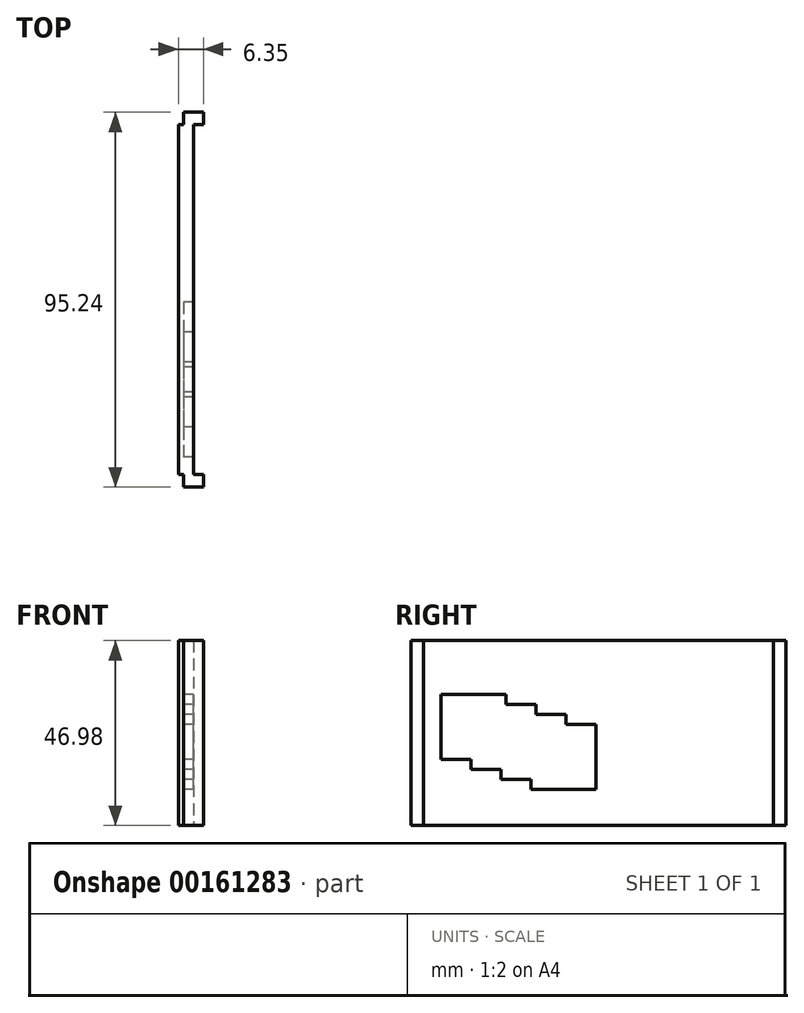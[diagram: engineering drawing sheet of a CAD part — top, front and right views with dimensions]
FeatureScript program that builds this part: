
annotation { "Feature Type Name" : "Feature", "Feature Type Description" : "" }
export const myFeature = defineFeature(function(context is Context, id is Id, definition is map)
    precondition{}
    {
        {
            var Q0;
            Q0=qCreatedBy(makeId("Right.planeOp"),FACE);
            var sketch = newSketch(context, id + "F0", { "sketchPlane" : qUnion([Q0])});
            skLineSegment(sketch, "E0.bottom", {"start": v(47.62, 23.5) * mm, "end": v(-47.63, 23.5) * mm});
            skLineSegment(sketch, "E0.top", {"start": v(47.63, -23.5) * mm, "end": v(-47.62, -23.5) * mm});
            skLineSegment(sketch, "E0.left", {"start": v(47.62, 23.5) * mm, "end": v(47.63, -23.5) * mm});
            skLineSegment(sketch, "E0.right", {"start": v(-47.63, 23.5) * mm, "end": v(-47.62, -23.5) * mm});
            skPoint(sketch, "E0.middle", {"position": v(0, 0) * mm});
            skLineSegment(sketch, "E1.bottom", {"start": v(-0.64, -14.35) * mm, "end": v(-17.14, -14.35) * mm});
            skLineSegment(sketch, "E1.top", {"start": v(-0.64, 2.16) * mm, "end": v(-17.15, 2.16) * mm});
            skLineSegment(sketch, "E1.left", {"start": v(-0.64, -14.35) * mm, "end": v(-0.64, 2.16) * mm});
            skLineSegment(sketch, "E1.right", {"start": v(-17.14, -14.35) * mm, "end": v(-17.15, 2.16) * mm});
            skPoint(sketch, "E1.middle", {"position": v(-8.9, -6.1) * mm});
            skLineSegment(sketch, "E2.bottom", {"start": v(-8.25, -11.81) * mm, "end": v(-24.77, -11.81) * mm});
            skLineSegment(sketch, "E2.top", {"start": v(-8.25, 4.7) * mm, "end": v(-24.77, 4.7) * mm});
            skLineSegment(sketch, "E2.left", {"start": v(-8.25, -11.81) * mm, "end": v(-8.25, 4.7) * mm});
            skLineSegment(sketch, "E2.right", {"start": v(-24.76, -11.81) * mm, "end": v(-24.77, 4.7) * mm});
            skLineSegment(sketch, "E3.bottom", {"start": v(-15.87, -9.27) * mm, "end": v(-32.38, -9.27) * mm});
            skLineSegment(sketch, "E3.top", {"start": v(-15.87, 7.24) * mm, "end": v(-32.38, 7.24) * mm});
            skLineSegment(sketch, "E3.left", {"start": v(-15.87, -9.27) * mm, "end": v(-15.87, 7.24) * mm});
            skLineSegment(sketch, "E3.right", {"start": v(-32.38, -9.27) * mm, "end": v(-32.38, 7.24) * mm});
            skLineSegment(sketch, "E4.bottom", {"start": v(-23.5, -6.73) * mm, "end": v(-40, -6.73) * mm});
            skLineSegment(sketch, "E4.top", {"start": v(-23.5, 9.78) * mm, "end": v(-40, 9.78) * mm});
            skLineSegment(sketch, "E4.left", {"start": v(-23.5, -6.73) * mm, "end": v(-23.5, 9.78) * mm});
            skLineSegment(sketch, "E4.right", {"start": v(-40, -6.73) * mm, "end": v(-40, 9.78) * mm});
            skSolve(sketch);
        }
        {
            var Q0;
            Q0=makeQuery(id+"F0.imprint","IMPRINT",FACE,{"disambiguationData":[TD([[makeQuery(id+"F0.imprint","IMPRINT",EDGE,{"derivedFrom":sQuery(id+"F0.wireOp",EDGE,"E0.bottom")}),1.0]])]});
            extrude(context, id + "F1", {"entities" : qUnion([Q0]), "depth" : 2.54 * mm});
        }
        {
            var Q0;
            Q0=makeQuery(id+"F1.opExtrude","CAP_FACE",FACE,{"disambiguationData":[OSD([sQuery(id+"F0.wireOp",EDGE,"E0.bottom"),sQuery(id+"F0.wireOp",EDGE,"E0.top"),sQuery(id+"F0.wireOp",EDGE,"E0.left"),sQuery(id+"F0.wireOp",EDGE,"E0.right"),sQuery(id+"F0.wireOp",EDGE,"E1.bottom"),sQuery(id+"F0.wireOp",EDGE,"E1.top"),sQuery(id+"F0.wireOp",EDGE,"E1.right"),sQuery(id+"F0.wireOp",EDGE,"db3a154d-421c-442b-b8d2-4df29128a182.bottom"),sQuery(id+"F0.wireOp",EDGE,"db3a154d-421c-442b-b8d2-4df29128a182.top"),sQuery(id+"F0.wireOp",EDGE,"db3a154d-421c-442b-b8d2-4df29128a182.left"),sQuery(id+"F0.wireOp",EDGE,"db3a154d-421c-442b-b8d2-4df29128a182.right"),sQuery(id+"F0.wireOp",EDGE,"fd7c79ed-5d07-4375-ac7c-8445cbfff98b.bottom"),sQuery(id+"F0.wireOp",EDGE,"fd7c79ed-5d07-4375-ac7c-8445cbfff98b.top"),sQuery(id+"F0.wireOp",EDGE,"fd7c79ed-5d07-4375-ac7c-8445cbfff98b.left"),sQuery(id+"F0.wireOp",EDGE,"fd7c79ed-5d07-4375-ac7c-8445cbfff98b.right"),sQuery(id+"F0.wireOp",EDGE,"f020ca0c-2cd2-49f9-a436-e8fc56810917.bottom"),sQuery(id+"F0.wireOp",EDGE,"f020ca0c-2cd2-49f9-a436-e8fc56810917.top"),sQuery(id+"F0.wireOp",EDGE,"f020ca0c-2cd2-49f9-a436-e8fc56810917.left"),sQuery(id+"F0.wireOp",EDGE,"f020ca0c-2cd2-49f9-a436-e8fc56810917.right")])],"isStart":true});
            var sketch = newSketch(context, id + "F2", { "sketchPlane" : qUnion([Q0])});
            skLineSegment(sketch, "E5.bottom", {"start": v(44.45, 23.5) * mm, "end": v(-44.45, 23.5) * mm});
            skLineSegment(sketch, "E5.top", {"start": v(44.45, -23.5) * mm, "end": v(-44.45, -23.5) * mm});
            skLineSegment(sketch, "E5.left", {"start": v(44.45, 23.5) * mm, "end": v(44.45, -23.5) * mm});
            skLineSegment(sketch, "E5.right", {"start": v(-44.45, 23.5) * mm, "end": v(-44.45, -23.5) * mm});
            skPoint(sketch, "E5.middle", {"position": v(0, 0) * mm});
            skSolve(sketch);
        }
        {
            var Q0;
            Q0=makeQuery(id+"F2.imprint","IMPRINT",FACE,{"disambiguationData":[TD([[makeQuery(id+"F2.imprint","IMPRINT",EDGE,{"derivedFrom":sQuery(id+"F2.wireOp",EDGE,"E5.bottom")}),-1.0]])]});
            var Q1;
            {var subQ2=sQuery(id+"F0.wireOp",EDGE,"E1.bottom");Q1=makeQuery(id+"F2.imprint","IMPRINT",FACE,{"disambiguationData":[TD([[makeQuery(id+"F2.imprint","IMPRINT",EDGE,{"derivedFrom":makeQuery(id+"F1.opExtrude","CAP_EDGE",EDGE,{"disambiguationData":[OSD([subQ2])],"isStart":true})}),1.0]])]});}
            extrude(context, id + "F3", {"entities" : qUnion([Q0, Q1]), "operationType" : NewBodyOperationType.ADD, "depth" : 1.27 * mm});
        }
        {
            var Q0;
            Q0=makeQuery(id+"F1.opExtrude","CAP_FACE",FACE,{"disambiguationData":[OSD([sQuery(id+"F0.wireOp",EDGE,"E0.bottom"),sQuery(id+"F0.wireOp",EDGE,"E0.top"),sQuery(id+"F0.wireOp",EDGE,"E0.left"),sQuery(id+"F0.wireOp",EDGE,"E0.right"),sQuery(id+"F0.wireOp",EDGE,"E1.bottom"),sQuery(id+"F0.wireOp",EDGE,"E1.top"),sQuery(id+"F0.wireOp",EDGE,"E1.right"),sQuery(id+"F0.wireOp",EDGE,"db3a154d-421c-442b-b8d2-4df29128a182.bottom"),sQuery(id+"F0.wireOp",EDGE,"db3a154d-421c-442b-b8d2-4df29128a182.top"),sQuery(id+"F0.wireOp",EDGE,"db3a154d-421c-442b-b8d2-4df29128a182.left"),sQuery(id+"F0.wireOp",EDGE,"db3a154d-421c-442b-b8d2-4df29128a182.right"),sQuery(id+"F0.wireOp",EDGE,"fd7c79ed-5d07-4375-ac7c-8445cbfff98b.bottom"),sQuery(id+"F0.wireOp",EDGE,"fd7c79ed-5d07-4375-ac7c-8445cbfff98b.top"),sQuery(id+"F0.wireOp",EDGE,"fd7c79ed-5d07-4375-ac7c-8445cbfff98b.left"),sQuery(id+"F0.wireOp",EDGE,"fd7c79ed-5d07-4375-ac7c-8445cbfff98b.right"),sQuery(id+"F0.wireOp",EDGE,"f020ca0c-2cd2-49f9-a436-e8fc56810917.bottom"),sQuery(id+"F0.wireOp",EDGE,"f020ca0c-2cd2-49f9-a436-e8fc56810917.top"),sQuery(id+"F0.wireOp",EDGE,"f020ca0c-2cd2-49f9-a436-e8fc56810917.left"),sQuery(id+"F0.wireOp",EDGE,"f020ca0c-2cd2-49f9-a436-e8fc56810917.right")])],"isStart":false});
            var sketch = newSketch(context, id + "F4", { "sketchPlane" : qUnion([Q0])});
            skLineSegment(sketch, "E6.bottom", {"start": v(-47.63, 23.5) * mm, "end": v(47.63, 23.5) * mm});
            skLineSegment(sketch, "E6.top", {"start": v(-47.63, -23.5) * mm, "end": v(47.63, -23.5) * mm});
            skLineSegment(sketch, "E6.left", {"start": v(-47.63, 23.5) * mm, "end": v(-47.63, -23.5) * mm});
            skLineSegment(sketch, "E6.right", {"start": v(47.63, 23.5) * mm, "end": v(47.63, -23.5) * mm});
            skLineSegment(sketch, "E7.bottom", {"start": v(-47.63, 23.5) * mm, "end": v(-44.45, 23.5) * mm});
            skLineSegment(sketch, "E7.top", {"start": v(-47.63, -23.5) * mm, "end": v(-44.45, -23.5) * mm});
            skLineSegment(sketch, "E7.right", {"start": v(-44.45, 23.5) * mm, "end": v(-44.45, -23.5) * mm});
            skLineSegment(sketch, "E8.bottom", {"start": v(47.63, 23.5) * mm, "end": v(44.45, 23.5) * mm});
            skLineSegment(sketch, "E8.top", {"start": v(47.63, -23.5) * mm, "end": v(44.45, -23.5) * mm});
            skLineSegment(sketch, "E8.right", {"start": v(44.45, 23.5) * mm, "end": v(44.45, -23.5) * mm});
            skSolve(sketch);
        }
        {
            var Q0;
            Q0=makeQuery(id+"F4.imprint","IMPRINT",FACE,{"disambiguationData":[TD([[makeQuery(id+"F4.imprint","IMPRINT",EDGE,{"derivedFrom":sQuery(id+"F4.wireOp",EDGE,"E6.bottom")}),1.0]])]});
            extrude(context, id + "F5", {"entities" : qUnion([Q0]), "operationType" : NewBodyOperationType.ADD, "depth" : 2.54 * mm});
        }
    });
